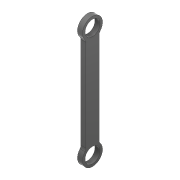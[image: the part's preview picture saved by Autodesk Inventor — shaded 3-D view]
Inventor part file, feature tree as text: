
AUTODESK INVENTOR PART (.ipt)
format: ipt  version: 2020 (Build 240168000, 168)  size: 105,984 bytes
history: native  units: mm
features: extrude x1, fillet x1, sketch x1
ambient origin geometry x8: Origin, YZ Plane, XZ Plane, XY Plane, X Axis, Y Axis, Z Axis, Center Point
bodies: Solid1 (feature_tree)
feature tree (3):
  extrude  "Extrusion1"  Depth=4.0mm
  fillet  "Fillet1"  Radius=110.0mm
  sketch  "Sketch1"  dims[d0=20.0mm d1=15.0mm d4=110.0mm d5=6.5mm d6=20.0mm d8=110.0mm d9=10.0mm d11=10.0mm d13=5.0mm d14=0.0mm d15=4.0mm d16=0.872665mm]
